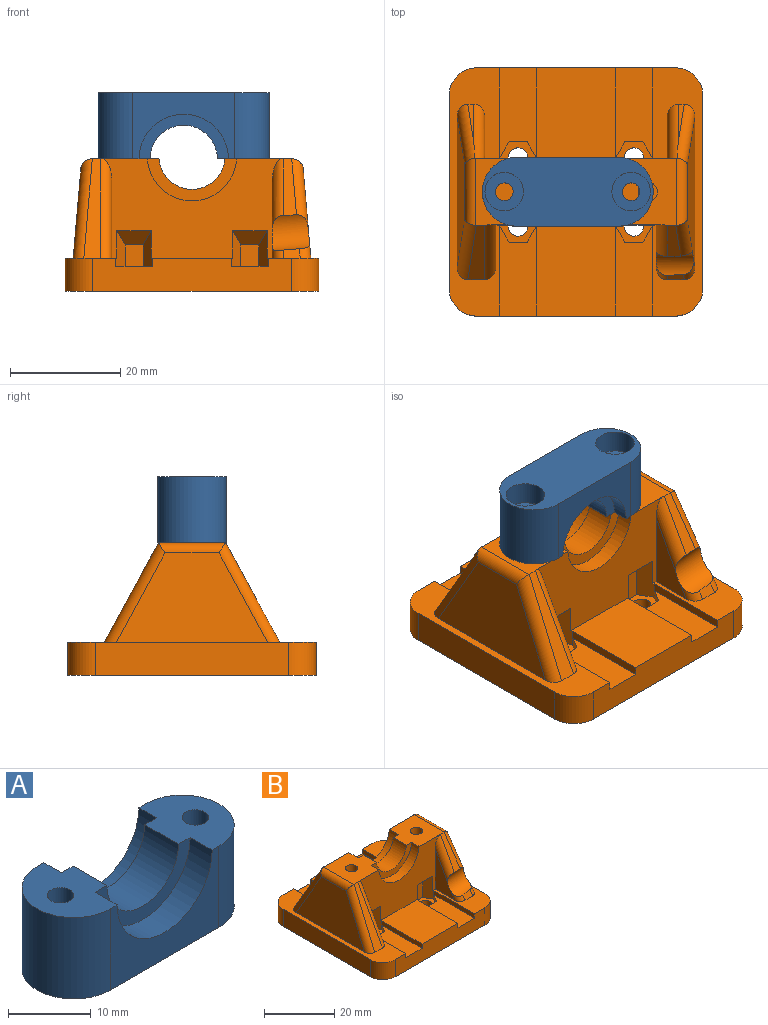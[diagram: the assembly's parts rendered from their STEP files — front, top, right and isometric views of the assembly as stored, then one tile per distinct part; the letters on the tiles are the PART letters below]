
ASSEMBLY  parts=2 mates=1
PART A: 18 faces, bbox 31x12.5x12 mm
  f0: cylinder r=1.6mm len=7.8mm, axis (0,0,-1), area 78.4mm2, adj f3,f17
  f1: cylinder r=1.6mm len=7.8mm, axis (0,0,-1), area 78.4mm2, adj f4,f15
  f2: plane 31x12.5mm, normal (0,0,-1), area 277mm2, adj f5,f7,f8,f9,f14,f16
  f3: plane 12.5x9.4mm, normal (0,0,1), area 79.2mm2, adj f0,f5,f6,f7,f9,f10,f11,f12
  f4: plane 12.5x9.4mm, normal (0,0,1), area 79.2mm2, adj f1,f5,f6,f8,f9,f10,f11,f12
  f5: plane 18.5x12mm, normal (0,-1,0), area 118.9mm2, adj f2,f3,f4,f7,f8,f12
  f6: cylinder r=6.1mm len=12.2mm, axis (0,1,0), area 110.2mm2, adj f3,f4,f11,f13
  f7: cylinder r=6.25mm len=12.5mm, axis (0,0,-1), area 235.6mm2, adj f2,f3,f5,f9
  f8: cylinder r=6.25mm len=12.5mm, axis (0,0,-1), area 235.6mm2, adj f2,f4,f5,f9
  f9: plane 18.5x12mm, normal (0,1,0), area 118.9mm2, adj f2,f3,f4,f7,f8,f10
  f10: cylinder r=8.1mm len=16.2mm, axis (0,1,0), area 76.3mm2, adj f3,f4,f9,f11
  f11: plane 16.2x8.1mm, normal (0,1,0), area 44.6mm2, adj f3,f4,f6,f10
  f12: cylinder r=8.1mm len=16.2mm, axis (0,-1,0), area 95.4mm2, adj f3,f4,f5,f13
  f13: plane 16.2x8.1mm, normal (0,-1,0), area 44.6mm2, adj f3,f4,f6,f12
  f14: cylinder r=3.5mm len=7mm, axis (0,0,-1), area 92.4mm2, adj f2,f15
  f15: plane 7x7mm, normal (0,0,-1), area 30.4mm2, adj f1,f14
  f16: cylinder r=3.5mm len=7mm, axis (0,0,-1), area 92.4mm2, adj f2,f17
  f17: plane 7x7mm, normal (0,0,-1), area 30.4mm2, adj f0,f16
PART B: 114 faces, bbox 46x45x24.1 mm
  f0: plane 14.03x7.66mm, normal (-1,0,0), area 53mm2, adj f3,f6,f22,f88,f113
  f1: plane 10.26x5.6mm, normal (0,-0.88,0.48), area 22.9mm2, adj f3,f26,f84,f113
  f2: cylinder r=2mm len=4.95mm, axis (0.08,-0.48,-0.88), area 7.2mm2, adj f6,f52,f74,f113
  f3: cylinder r=2mm len=13.28mm, axis (0,0.48,0.88), area 35.1mm2, adj f0,f1,f22,f26,f113
  f4: plane 45x9.35mm, normal (0,0,1), area 195.5mm2, adj f8,f21,f22,f27,f28,f36,f49,f51
  f5: plane 16.5x14.71mm, normal (0,0,1), area 237.9mm2, adj f8,f21,f35,f39,f101,f103,f106
  f6: plane 45x9.35mm, normal (0,0,1), area 195.5mm2, adj f0,f2,f8,f21,f22,f28,f29,f41
  f7: plane 16.5x14.71mm, normal (0,0,1), area 237.9mm2, adj f22,f28,f45,f47,f95,f98
  f8: plane 36x6mm, normal (0,1,0), area 196.3mm2, adj f4,f5,f6,f30,f92,f93,f102,f103
  f9: plane 2.85x1.65mm, normal (-0.87,-0.5,0), area 4.9mm2, adj f10,f35,f38,f108
  f10: plane 3.29x1.5mm, normal (0,-1,0), area 4.9mm2, adj f9,f11,f38,f108
  f11: plane 2.85x1.65mm, normal (0.87,-0.5,0), area 4.9mm2, adj f10,f36,f38,f108
  f12: plane 3.29x1.5mm, normal (0,-1,0), area 4.9mm2, adj f13,f14,f42,f104
  f13: plane 2.85x1.65mm, normal (0.87,-0.5,0), area 4.9mm2, adj f12,f39,f42,f104
  f14: plane 2.85x1.65mm, normal (-0.87,-0.5,0), area 4.9mm2, adj f12,f41,f42,f104
  f15: plane 2.85x1.65mm, normal (0.87,0.5,0), area 4.9mm2, adj f16,f45,f46,f100
  f16: plane 3.29x1.5mm, normal (0,1,0), area 4.9mm2, adj f15,f17,f46,f100
  f17: plane 2.85x1.65mm, normal (-0.87,0.5,0), area 4.9mm2, adj f16,f43,f46,f100
  f18: plane 3.29x1.5mm, normal (0,1,0), area 4.9mm2, adj f19,f20,f50,f97
  f19: plane 2.85x1.65mm, normal (-0.87,0.5,0), area 4.9mm2, adj f18,f47,f50,f97
  f20: plane 2.85x1.65mm, normal (0.87,0.5,0), area 4.9mm2, adj f18,f49,f50,f97
  f21: plane 35.91x18mm, normal (0,1,0), area 375.9mm2, adj f4,f5,f6,f26,f35,f36,f39,f41
  f22: plane 31.91x18mm, normal (0,-1,0), area 368.7mm2, adj f0,f3,f4,f6,f7,f26,f43,f45
  f23: cylinder r=1.75mm len=5mm, axis (0,0,1), area 55mm2, adj f53,f66
  f24: cylinder r=1.75mm len=5mm, axis (0,0,1), area 55mm2, adj f26,f59
  f25: cylinder r=6.01mm len=11.98mm, axis (0,1,0), area 94.8mm2, adj f26,f53,f55,f57
  f26: plane 12.2x12.18mm, normal (0,0,1), area 122.6mm2, adj f1,f3,f21,f22,f24,f25,f54,f55
  f27: plane 35x6mm, normal (-1,0,0), area 210mm2, adj f4,f30,f90,f93
  f28: plane 36x6mm, normal (0,-1,0), area 196.3mm2, adj f4,f6,f7,f30,f90,f91,f95,f96
  f29: plane 35x6mm, normal (1,0,0), area 210mm2, adj f6,f30,f91,f92
  f30: plane 46x45mm, normal (0,0,-1), area 2010.1mm2, adj f8,f27,f28,f29,f31,f32,f33,f34
  f31: cylinder r=1.75mm len=3.5mm, axis (0,0,1), area 33mm2, adj f30,f38
  f32: cylinder r=1.75mm len=3.5mm, axis (0,0,1), area 33mm2, adj f30,f42
  f33: cylinder r=1.75mm len=3.5mm, axis (0,0,1), area 33mm2, adj f30,f46
  f34: cylinder r=1.75mm len=3.5mm, axis (0,0,1), area 33mm2, adj f30,f50
  f35: plane 8x2.85mm, normal (-0.87,0.5,0), area 21mm2, adj f5,f9,f21,f37,f38,f106,f111
  f36: plane 8x2.85mm, normal (0.87,0.5,0), area 21mm2, adj f4,f11,f21,f37,f38,f105,f111
  f37: plane 5.4x3.29mm, normal (0,1,0), area 17.8mm2, adj f35,f36,f38,f111
  f38: plane 6.58x5.7mm, normal (0,0,1), area 18.5mm2, adj f9,f10,f11,f31,f35,f36,f37
  f39: plane 8x2.85mm, normal (0.87,0.5,0), area 21mm2, adj f5,f13,f21,f40,f42,f101,f112
  f40: plane 5.4x3.29mm, normal (0,1,0), area 17.8mm2, adj f39,f41,f42,f112
  f41: plane 8x2.85mm, normal (-0.87,0.5,0), area 21mm2, adj f6,f14,f21,f40,f42,f102,f112
  f42: plane 6.58x5.7mm, normal (0,0,1), area 18.5mm2, adj f12,f13,f14,f32,f39,f40,f41
  f43: plane 8x2.85mm, normal (-0.87,-0.5,0), area 21mm2, adj f6,f17,f22,f44,f46,f99,f109
  f44: plane 5.4x3.29mm, normal (0,-1,0), area 17.8mm2, adj f43,f45,f46,f109
  f45: plane 8x2.85mm, normal (0.87,-0.5,0), area 21mm2, adj f7,f15,f22,f44,f46,f98,f109
  f46: plane 6.58x5.7mm, normal (0,0,1), area 18.5mm2, adj f15,f16,f17,f33,f43,f44,f45
  f47: plane 8x2.85mm, normal (-0.87,-0.5,0), area 21mm2, adj f7,f19,f22,f48,f50,f95,f110
  f48: plane 5.4x3.29mm, normal (0,-1,0), area 17.8mm2, adj f47,f49,f50,f110
  f49: plane 8x2.85mm, normal (0.87,-0.5,0), area 21mm2, adj f4,f20,f22,f48,f50,f96,f110
  f50: plane 6.58x5.7mm, normal (0,0,1), area 18.5mm2, adj f18,f19,f20,f34,f47,f48,f49
  f51: plane 27.46x16.17mm, normal (-1,0,0.09), area 302.6mm2, adj f4,f81,f82,f83
  f52: plane 27.46x16.17mm, normal (1,0,0.09), area 302.5mm2, adj f2,f6,f84,f85,f86,f113
  f53: plane 12.2x12.18mm, normal (0,0,1), area 122.6mm2, adj f21,f22,f23,f25,f54,f55,f56,f57
  f54: cylinder r=8.1mm len=16.17mm, axis (0,1,0), area 90.5mm2, adj f21,f26,f53,f55
  f55: plane 16.17x7.6mm, normal (0,1,0), area 44.2mm2, adj f25,f26,f53,f54
  f56: cylinder r=8.1mm len=16.17mm, axis (0,-1,0), area 73.3mm2, adj f22,f26,f53,f57
  f57: plane 16.17x7.6mm, normal (0,-1,0), area 44.2mm2, adj f25,f26,f53,f56
  f58: plane 11.5x7.3mm, normal (0,0,1), area 74.3mm2, adj f21,f60,f61,f62,f64,f75
  f59: plane 11.5x7.3mm, normal (0,0,-1), area 74.3mm2, adj f21,f24,f60,f61,f62,f75
  f60: plane 11.5x4.5mm, normal (-1,0,0), area 51.8mm2, adj f58,f59,f62,f75
  f61: plane 11.5x4.5mm, normal (1,0,0), area 51.8mm2, adj f21,f58,f59,f62
  f62: plane 7.3x4.5mm, normal (0,1,0), area 32.9mm2, adj f58,f59,f60,f61
  f63: plane 3.5x3.5mm, normal (0,0,1), area 9.6mm2, adj f64
  f64: cylinder r=1.75mm len=5.5mm, axis (0,0,1), area 60.5mm2, adj f58,f63
  f65: plane 11.5x7.3mm, normal (0,0,1), area 74.3mm2, adj f21,f67,f68,f69,f71,f78
  f66: plane 11.5x7.3mm, normal (0,0,-1), area 74.3mm2, adj f21,f23,f67,f68,f69,f78
  f67: plane 11.5x4.5mm, normal (-1,0,0), area 51.7mm2, adj f21,f65,f66,f69
  f68: plane 11.5x4.5mm, normal (1,0,0), area 51.7mm2, adj f65,f66,f69,f78
  f69: plane 7.3x4.5mm, normal (0,1,0), area 32.9mm2, adj f65,f66,f67,f68
  f70: plane 3.5x3.5mm, normal (0,0,1), area 9.6mm2, adj f71
  f71: cylinder r=1.75mm len=5.5mm, axis (0,0,1), area 60.5mm2, adj f65,f70
  f72: plane 14.01x7.64mm, normal (1,0,0), area 53.5mm2, adj f4,f22,f89
  f73: plane 18x9.81mm, normal (0,-0.88,0.48), area 47.2mm2, adj f4,f53,f81,f89
  f74: plane 3.09x1.74mm, normal (0,-0.88,0.48), area 5.5mm2, adj f2,f6,f88,f113
  f75: plane 4.5x0.11mm, normal (0,-1,0), area 0.5mm2, adj f58,f59,f60,f76
  f76: plane 14.01x7.64mm, normal (-1,0,0), area 53.5mm2, adj f6,f21,f75,f87
  f77: plane 12.54x6.84mm, normal (0,0.88,0.48), area 7.7mm2, adj f6,f85,f87
  f78: plane 4.5x0.11mm, normal (0,-1,0), area 0.5mm2, adj f65,f66,f68,f79
  f79: plane 14.01x7.64mm, normal (1,0,0), area 53.5mm2, adj f4,f21,f78,f94
  f80: plane 12.54x6.84mm, normal (0,0.88,0.48), area 7.7mm2, adj f4,f83,f94
  f81: cylinder r=2mm len=18.81mm, axis (-0.08,-0.48,-0.88), area 60.7mm2, adj f4,f51,f53,f73,f82
  f82: cylinder r=2mm len=12.19mm, axis (0,-1,0), area 33.5mm2, adj f51,f53,f81,f83,f94
  f83: cylinder r=2mm len=18.79mm, axis (-0.08,0.48,-0.88), area 59.9mm2, adj f4,f51,f80,f82,f94
  f84: cylinder r=2mm len=13.36mm, axis (0.08,-0.48,-0.88), area 36.2mm2, adj f1,f26,f52,f86,f113
  f85: cylinder r=2mm len=18.79mm, axis (0.08,0.48,-0.88), area 59.9mm2, adj f6,f52,f77,f86,f87
  f86: cylinder r=2mm len=12.19mm, axis (0,-1,0), area 33.5mm2, adj f26,f52,f84,f85,f87
  f87: cylinder r=2mm len=19mm, axis (0,0.48,-0.88), area 58.8mm2, adj f6,f21,f26,f76,f77,f85,f86
  f88: cylinder r=2mm len=4.18mm, axis (0,0.48,0.88), area 5.5mm2, adj f0,f6,f74,f113
  f89: cylinder r=2mm len=19mm, axis (0,-0.48,-0.88), area 59.6mm2, adj f4,f22,f53,f72,f73
  f90: cylinder r=5mm len=6mm, axis (0,0,-1), area 47.1mm2, adj f4,f27,f28,f30
  f91: cylinder r=5mm len=6mm, axis (0,0,1), area 47.1mm2, adj f6,f28,f29,f30
  f92: cylinder r=5mm len=6mm, axis (0,0,-1), area 47.1mm2, adj f6,f8,f29,f30
  f93: cylinder r=5mm len=6mm, axis (0,0,1), area 47.1mm2, adj f4,f8,f27,f30
  f94: cylinder r=2mm len=19mm, axis (0,-0.48,0.88), area 58.8mm2, adj f4,f21,f53,f79,f80,f82,f83
  f95: plane 16.25x1.5mm, normal (-1,0,0), area 24.4mm2, adj f7,f28,f47,f97
  f96: plane 16.25x1.5mm, normal (1,0,0), area 24.4mm2, adj f4,f28,f49,f97
  f97: plane 16.25x6.58mm, normal (0,0,1), area 92.9mm2, adj f18,f19,f20,f28,f95,f96
  f98: plane 16.25x1.5mm, normal (1,0,0), area 24.4mm2, adj f7,f28,f45,f100
  f99: plane 16.25x1.5mm, normal (-1,0,0), area 24.4mm2, adj f6,f28,f43,f100
  f100: plane 16.25x6.58mm, normal (0,0,1), area 92.9mm2, adj f15,f16,f17,f28,f98,f99
  f101: plane 1.5x0mm, normal (0,1,0), area 0mm2, adj f5,f39,f103,f104
  f102: plane 16.25x1.5mm, normal (-1,0,0), area 24.4mm2, adj f6,f8,f41,f104
  f103: plane 16.25x1.5mm, normal (1,0,0), area 24.4mm2, adj f5,f8,f101,f104
  f104: plane 16.25x6.58mm, normal (0,0,1), area 92.9mm2, adj f8,f12,f13,f14,f101,f102,f103
  f105: plane 1.5x0mm, normal (0,1,0), area 0mm2, adj f4,f36,f107,f108
  f106: plane 16.25x1.5mm, normal (-1,0,0), area 24.4mm2, adj f5,f8,f35,f108
  f107: plane 16.25x1.5mm, normal (1,0,0), area 24.4mm2, adj f4,f8,f105,f108
  f108: plane 16.25x6.58mm, normal (0,0,1), area 92.9mm2, adj f8,f9,f10,f11,f105,f106,f107
  f109: plane 6.29x2.6mm, normal (0,-0.71,-0.71), area 17.6mm2, adj f22,f43,f44,f45
  f110: plane 6.29x2.6mm, normal (0,-0.71,-0.71), area 17.6mm2, adj f22,f47,f48,f49
  f111: plane 6.29x2.6mm, normal (0,0.71,-0.71), area 17.6mm2, adj f21,f35,f36,f37
  f112: plane 6.29x2.6mm, normal (0,0.71,-0.71), area 17.6mm2, adj f21,f39,f40,f41
  f113: cylinder r=4mm len=7.3mm, axis (1,0,0.09), area 53.5mm2, adj f0,f1,f2,f3,f52,f74,f84,f88
PLACE A rot(axis=(1,0,0),180deg) t=(-3.58,17.14,38.13)mm
PLACE B t=(-2.08,17.14,2.13)mm
MATE fastened A.f0 <-> B.f23  axis (0,0,-1) through (-15.08,17.14,26.13)mm
